# Revit family: 180 series
name_source: partatom
category: Mechanical Equipment
revit_build: Autodesk Revit 2013 (Build: 20120221_2030(x64)
units: mm (PartAtom-declared; Revit-internal decimal feet)

## types (24) — shared parameters
Assembly Code = D2010900
Cooling = Oil Filled
Cord Length = 240"
Cord Type = UL listed, 3-wire neoprene cord and plug.
Default Elevation = 0"
Description = Single Seal High Head Commercial Effluent Pumps
Discharge Diameter = 1-1/2" NPT (optional 2" or 3" flange)
Discharge Height = 6"
Discharge Radius = 3/4"
Height = 19 5/16"
Hertz = 60
Impeller = Bronze
Impeller Type = Non-clogging vortex
Installation Type = Floor Mounted
Insulation = Class B
Lead Wires Insulation = Class B
Length = 12 3/4"
Manufacturer = Zoeller
Masterformat Number = 33 36 16
Masterformat Title = Utility Septic Tank Effluent Pumps
Material = Cast Iron-Zoeller-Powder Coated Epoxy
Max. Operating Temp. = 130.00 °F
Motor Thermal Shutoff (Single Phase Only) = Thermal Overload Sensors With Automatic Reset.
Motor Type = Submersible
Omniclass Table 23 Code = 23.60.30.21
Omniclass Table 23 Title = Pumps
Operation = Non-Automatic
Price = Prices may vary. Please consult Manufacturer Representative for most up-to-date price list.
Product Page URL = htthttp://www.zoellerpumps.com
RPM = 3450
Shaft Seal = Carbon and Ceramic
Solid Handling = 3/4" Spherical Solids
Square Ring & Gasket = Neoprene
Type Comments = Available in single or double seal designs.
URL = http://www.zoellerpumps.com
Warranty Information = 36 Months (Limited)
Waste Connection = Yes
Width = 8"

## per-type parameters (varying)
| type | Amps | Apparent Load | Flow 185 @ 30', 186-191 @ 5' | Maximum Head | Minimum Head = 360" | Model | Motor | Phase | Type | Voltage |
| 185-230V 1Ph | 10 A | 2254 VA | 85 GPM | 876" | Yes | 185 | 1 HP | 1 | Permanent Split Capacitor | 230 V |
| 185-200V 1Ph | 12 A | 2300 VA | 85 GPM | 876" | Yes | 185 | 1 HP | 1 | Permanent Split Capacitor | 200 V |
| 185-230V 3Ph | 7 A | 1702 VA | 85 GPM | 876" | Yes | 185 | 1 HP | 3 Ph | 3 Phase | 230 V |
| 185-200V 3Ph | 8 A | 1500 VA | 85 GPM | 876" | Yes | 185 | 1 HP | 3 Ph | 3 Phase | 200 V |
| 185-460V 3Ph | 4 A | 1702 VA | 85 GPM | 876" | Yes | 185 | 1 HP | 3 Ph | 3 Phase | 460 V |
| 185-575V 3Ph | 3 A | 1898 VA | 85 GPM | 876" | Yes | 185 | 1 HP | 3 Ph | 3 Phase | 575 V |
| 186-230V 1Ph | 14 A | 3151 VA | 58 GPM | 1368" | No | 186 | 1 1/2 HP | 1 | Split Capacitor | 230 V |
| 186-200V 1Ph | 17 A | 3440 VA | 58 GPM | 1368" | No | 186 | 1 1/2 HP | 1 | Split Capacitor | 200 V |
| 186-230V 3Ph | 9 A | 2116 VA | 58 GPM | 1368" | No | 186 | 1 1/2 HP | 3 Ph | 3 Phase | 230 V |
| 186-200V 3Ph | 10 A | 2060 VA | 58 GPM | 1368" | No | 186 | 1 1/2 HP | 3 Ph | 3 Phase | 200 V |
| 186-460V 3Ph | 5 A | 2116 VA | 58 GPM | 1368" | No | 186 | 1 1/2 HP | 3 Ph | 3 Phase | 460 V |
| 186-575V 3Ph | 4 A | 2070 VA | 58 GPM | 1368" | No | 186 | 1 1/2 HP | 3 Ph | 3 Phase | 575 V |
| 188-230V 1Ph | 14 A | 3220 VA | 145 GPM | 1092" | No | 188 | 1 1/2 HP | 1 | Permanent Split Capacitor | 230 V |
| 188-200V 1Ph | 17 A | 3360 VA | 145 GPM | 1092" | No | 188 | 1 1/2 HP | 1 | Permanent Split Capacitor | 200 V |
| 188-230V 3Ph | 9 A | 2047 VA | 145 GPM | 1092" | No | 188 | 1 1/2 HP | 3 Ph | 3 Phase | 230 V |
| 188-200V 3Ph | 21 A | 4100 VA | 145 GPM | 1092" | No | 188 | 1 1/2 HP | 3 Ph | 3 Phase | 200 V |
| 188-460V 3Ph | 5 A | 2116 VA | 145 GPM | 1092" | No | 188 | 1 1/2 HP | 3 Ph | 3 Phase | 460 V |
| 188-575V 3Ph | 4 A | 2013 VA | 145 GPM | 1092" | No | 188 | 1 1/2 HP | 3 Ph | 3 Phase | 575 V |
| 189-230V 1Ph | 17 A | 3933 VA | 145 GPM | 1320" | No | 189 | 2 HP | 1 | Permanent Split Capacitor | 230 V |
| 189-200V 1Ph | 21 A | 4100 VA | 145 GPM | 1320" | No | 189 | 2 HP | 1 | Permanent Split Capacitor | 200 V |
| 189-230V 3Ph | 11 A | 2576 VA | 145 GPM | 1320" | No | 189 | 2 HP | 3 Ph | 3 Phase | 230 V |
| 189-200V 3Ph | 13 A | 2640 VA | 145 GPM | 1320" | No | 189 | 2 HP | 3 Ph | 3 Phase | 200 V |
| 189-460V 3Ph | 6 A | 2760 VA | 145 GPM | 1320" | No | 189 | 2 HP | 3 Ph | 3 Phase | 460 V |
| 189-575V 3Ph | 6 A | 3335 VA | 145 GPM | 1320" | No | 189 | 2 HP | 3 Ph | 3 Phase | 575 V |

## geometry (parser evidence)
native form markers: Blend x6, Sweep x1
no freeform markers — native parametric forms only
